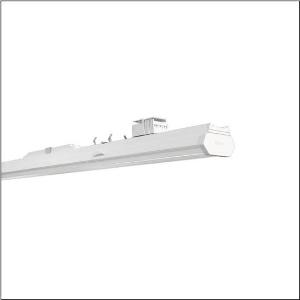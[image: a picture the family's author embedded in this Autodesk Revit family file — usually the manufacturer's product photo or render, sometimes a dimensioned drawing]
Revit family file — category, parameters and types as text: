
# Revit family: licross_r__11_protected_ho_51tp13mn4gxs_4b4b
name_source: partatom
category: Lighting Fixtures
units: mm (PartAtom-declared; Revit-internal decimal feet)

## family parameters
Cut with Voids When Loaded = No
Host = Face
Light Source = No
Part Type = Normal
Room Calculation Point = No
Round Connector Dimension = Use Diameter
Shared = No

## types (1)
- --- (1 x LED, 16110 lm, 87.4 W, 4000K)
    Apparent Load = 87 VA
    CIE Flux Codes = 89 96 99 100 99
    Color Rendering = 80
    Color Temperature = 4000K
    Default Elevation = 1800 mm
    Description = Licross® 11 Protected HO, luminaire insert, of sheet steel, galvanised, coil coated, white, length: 1.500mm, width: 90mm, height: 101mm, LED rated luminous flux: 16.110lm, light colour: 840, control gear: ON/OFF Multilumen, with plug, 3-pole, with phase selection, mains connection: 220..240V, AC, 50/60Hz, rated input power: 87W, halogen-free wiring, primary light control with lens, of plastic, primary optical cover: cover, of PMMA, light emission: direct distribution, primary light characteristic: symmetric, protection rating (complete): IP64, insulation class (complete): insulation class I (protective earthing), certification: CE, ENEC, VDE, UKCA, protection symbol: D if used in an environment with conductive dust loads with corresponding accessories, impact resistance: IK06, permissible ambient temperature for indoor applications: -35..+35°C, corresponds to IFS (International Featured Standards) requirements for safety and quality in the food industry, reducing of maximum allowable ambient temperature of 5°C with ceiling mounting, LABS conformity tested according to VDMA 24364:2018-05, packaging unit: 1 piece
    Height = 92 mm
    Lamp = 1 x LED
    Lamp Light Flux = 16110 lm
    Lamp Power = 87.4 W
    Lamp count = 1
    Length = 1500 mm
    Luminous efficacy = 184 lm/W
    Manufacturer = Siteco
    ModVariant = No
    Model = 51TP13MN4GXS
    Mounting Place = Ceiling
    Mounting Type = Pendant
    Number of Poles = 1
    OnlyDefault = Yes
    Power Factor = 1
    Product Name = Licross® 11 Protected HO
    Product group = luminaire insert
    ProductGroupID = 901
    Protection Class = Protection class I
    Protection Degree = IP 64
    RLX_Detail_Level = 1
    RLX_Emergency_Light_Flux = 0 lm
    RLX_Emergency_Type = 0
    RLX_Emergency_Type_DB = No
    RlxData = <blob elided: 21997 chars, md5=f71394b6>
    Socket = socket
    Standby Power = 0 W
    System Light Flux = 16110 lm
    System Power = 87 W
    Type Comments = factory setting: luminous flux: 100 % | (A | C | E) | 203 mA
    Type Image = l_1256148.jpg
    URL = http://relux.com
    VarID = @adj_037909
    Voltage = 0 V
    Weight = 0.00 kg
    Width = 88 mm

## geometry (parser evidence)
native form markers: Blend x4, Sweep x9
no freeform markers — native parametric forms only
